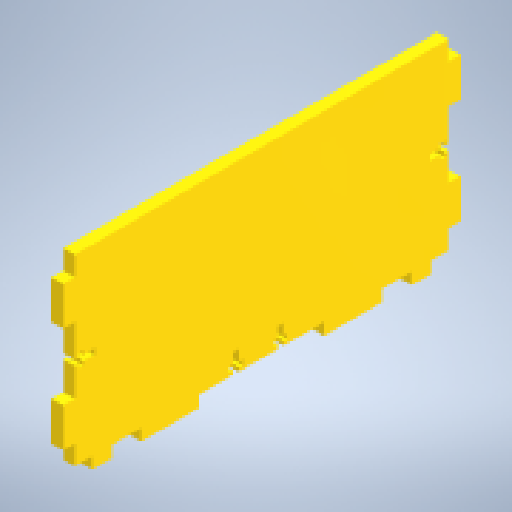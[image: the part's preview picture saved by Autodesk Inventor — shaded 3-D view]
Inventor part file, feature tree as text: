
AUTODESK INVENTOR PART (.ipt)
format: ipt  version: 2024.2 (Build 282272000, 272)  size: 268,288 bytes
history: native  units: mm
features: extrude x4, sketch x4, other x1
ambient origin geometry x8: Origin, YZ Plane, XZ Plane, XY Plane, X Axis, Y Axis, Z Axis, Center Point
bodies: Body1 (feature_tree)
feature tree (9):
  other  "Твердое тело1"
  extrude  "Выдавливание1"  Depth=204.0mm
  extrude  "Выдавливание2"  Depth=100.0mm
  extrude  "Выдавливание4"  Depth=40.0mm
  extrude  "Выдавливание5"  Depth=30.0mm
  sketch  "Эскиз1"
  sketch  "Эскиз2"
  sketch  "Эскиз4"
  sketch  "Эскиз6"
